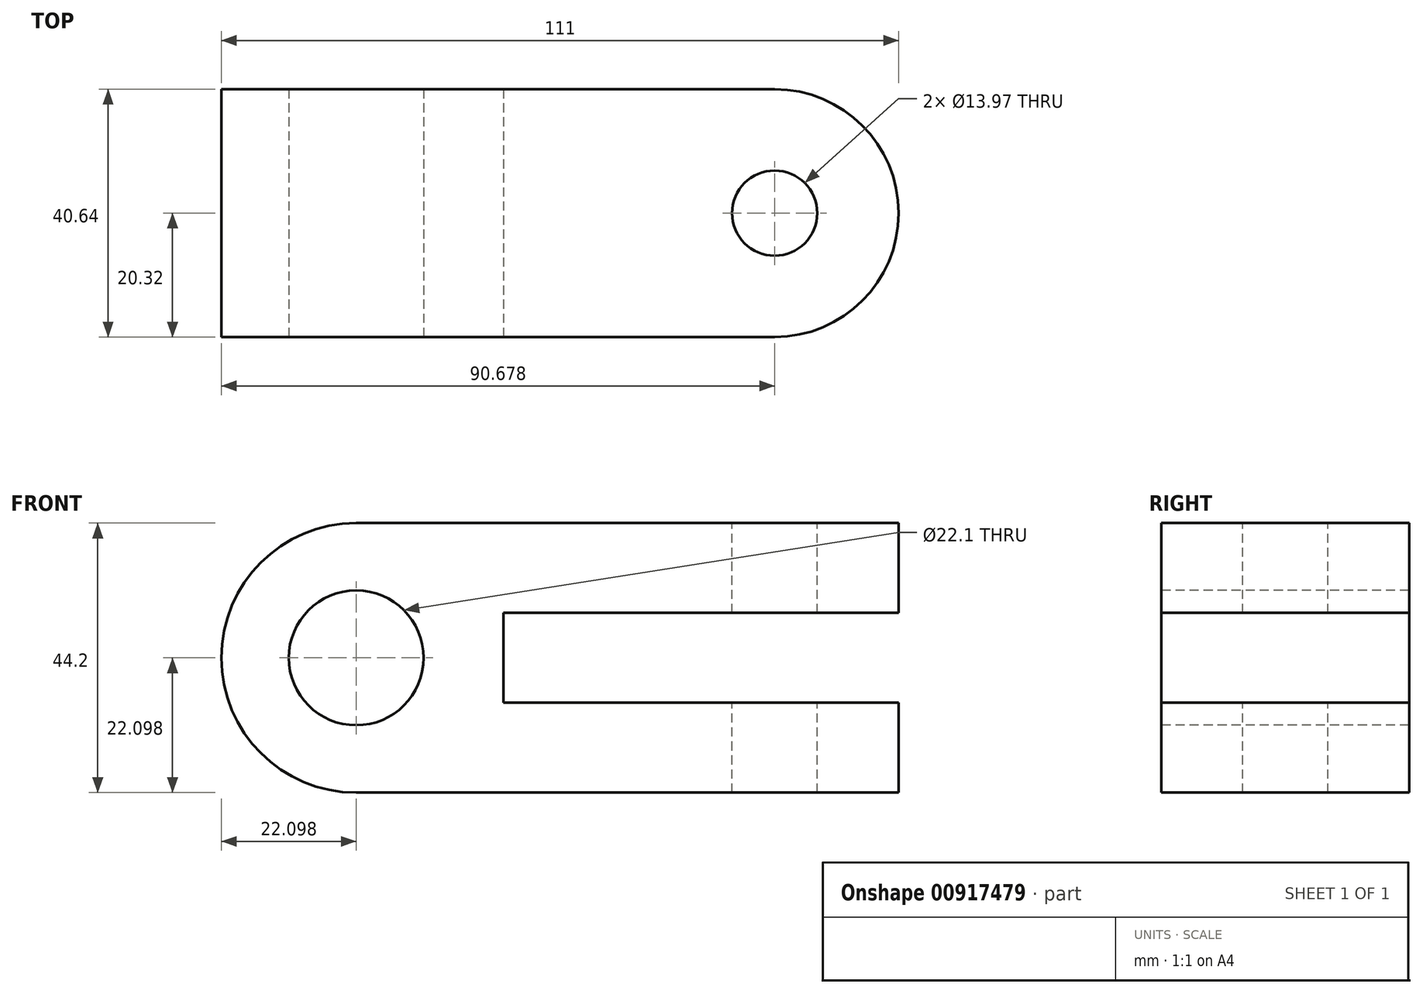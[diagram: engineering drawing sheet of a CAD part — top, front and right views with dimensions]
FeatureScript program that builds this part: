
annotation { "Feature Type Name" : "Feature", "Feature Type Description" : "" }
export const myFeature = defineFeature(function(context is Context, id is Id, definition is map)
    precondition{}
    {
        {
            var Q0;
            Q0=qCreatedBy(makeId("Top.planeOp"),FACE);
            var sketch = newSketch(context, id + "F0", { "sketchPlane" : qUnion([Q0])});
            skLineSegment(sketch, "E0.bottom", {"start": v(0, 0) * mm, "end": v(111, 0) * mm});
            skLineSegment(sketch, "E0.top", {"start": v(0, 40.64) * mm, "end": v(111, 40.64) * mm});
            skLineSegment(sketch, "E0.left", {"start": v(0, 0) * mm, "end": v(0, 40.64) * mm});
            skLineSegment(sketch, "E0.right", {"start": v(111, 0) * mm, "end": v(111, 40.64) * mm});
            skSolve(sketch);
        }
        {
            var Q0;
            Q0=makeQuery(id+"F0.imprint","IMPRINT",FACE,{"disambiguationData":[TD([[makeQuery(id+"F0.imprint","IMPRINT",EDGE,{"derivedFrom":sQuery(id+"F0.wireOp",EDGE,"E0.bottom")}),1.0]])]});
            extrude(context, id + "F1", {"entities" : qUnion([Q0]), "depth" : 44.2 * mm, "offsetDistance" : 25.4 * mm});
        }
        {
            var Q0;
            Q0=makeQuery(id+"F1.opExtrude","CAP_FACE",FACE,{"disambiguationData":[OSD([sQuery(id+"F0.wireOp",EDGE,"E0.bottom"),sQuery(id+"F0.wireOp",EDGE,"E0.top"),sQuery(id+"F0.wireOp",EDGE,"E0.left"),sQuery(id+"F0.wireOp",EDGE,"E0.right")])],"isStart":false});
            var sketch = newSketch(context, id + "F2", { "sketchPlane" : qUnion([Q0])});
            skCircle(sketch, "E1", {"center": v(90.68, 20.32) * mm, "radius": 20.32 * mm});
            skCircle(sketch, "E2", {"center": v(90.68, 20.32) * mm, "radius": 6.99 * mm});
            skSolve(sketch);
        }
        {
            var Q0;
            Q0=makeQuery(id+"F1.opExtrude","SWEPT_FACE",FACE,{"disambiguationData":[OSD([sQuery(id+"F0.wireOp",EDGE,"E0.bottom")])]});
            var sketch = newSketch(context, id + "F3", { "sketchPlane" : qUnion([Q0])});
            skCircle(sketch, "E3", {"center": v(22.1, 22.1) * mm, "radius": 22.1 * mm});
            skLineSegment(sketch, "E4", {"start": v(111, 29.46) * mm, "end": v(46.23, 29.46) * mm});
            skLineSegment(sketch, "E5", {"start": v(111, 14.73) * mm, "end": v(46.23, 14.73) * mm});
            skLineSegment(sketch, "E6", {"start": v(46.23, 14.73) * mm, "end": v(46.23, 29.62) * mm});
            skSolve(sketch);
        }
        {
            var Q0;
            Q0=makeQuery(id+"F1.opExtrude","SWEPT_FACE",FACE,{"disambiguationData":[OSD([sQuery(id+"F0.wireOp",EDGE,"E0.bottom")])]});
            var sketch = newSketch(context, id + "F4", { "sketchPlane" : qUnion([Q0])});
            skPoint(sketch, "E7", {"position": v(22.1, 22.1) * mm});
            skSolve(sketch);
        }
        {
            var Q0;
            Q0=sQuery(id+"F4.wireOp",VERTEX,"E7");
            var Q1;
            Q1=makeQuery(id+"F1.opExtrude","SWEPT_BODY",BODY,{"disambiguationData":[OSD([sQuery(id+"F0.wireOp",EDGE,"E0.bottom"),sQuery(id+"F0.wireOp",EDGE,"E0.top"),sQuery(id+"F0.wireOp",EDGE,"E0.left"),sQuery(id+"F0.wireOp",EDGE,"E0.right")])]});
            hole(context, id + "F5", {"style" : HoleStyle.SIMPLE, "endStyle" : HoleEndStyle.THROUGH, "holeDiameter" : 22.1 * mm, "majorDiameter" : 6.35 * mm, "isTappedThrough" : true, "tappedDepth" : 12.7 * mm, "tapClearance" : 3, "locations" : qUnion([Q0]), "scope" : qUnion([Q1])});
        }
        {
            var Q0;
            Q0=makeQuery(id+"F2.imprint","IMPRINT",FACE,{"disambiguationData":[TD([[makeQuery(id+"F2.imprint","IMPRINT",EDGE,{"derivedFrom":sQuery(id+"F2.wireOp",EDGE,"E2")}),1.0]])]});
            var Q1;
            Q1=sQuery(id+"F2.wireOp",EDGE,"E2");
            extrude(context, id + "F6", {"entities" : qUnion([Q0]), "operationType" : NewBodyOperationType.REMOVE, "surfaceEntities" : qUnion([Q1]), "endBound" : BoundingType.THROUGH_ALL, "oppositeDirection" : true, "depth" : 25.4 * mm, "offsetDistance" : 25.4 * mm});
        }
        {
            var Q0;
            {var subQ0=sQuery(id+"F2.wireOp",EDGE,"E1");var subQ1=makeQuery(id+"F1.opExtrude","CAP_EDGE",EDGE,{"disambiguationData":[OSD([sQuery(id+"F0.wireOp",EDGE,"E0.top")])],"isStart":false});var subQ2=makeQuery(id+"F2.imprint","INTERSECT",VERTEX,{"derivedFrom":[subQ1,subQ0]});Q0=makeQuery(id+"F2.imprint","IMPRINT",FACE,{"disambiguationData":[TD([[makeQuery(id+"F2.imprint","IMPRINT",EDGE,{"disambiguationData":[TD([[subQ2,1.0]])],"derivedFrom":subQ0}),-1.0]])]});}
            var Q1;
            {var subQ0=sQuery(id+"F2.wireOp",EDGE,"E1");var subQ1=makeQuery(id+"F1.opExtrude","CAP_EDGE",EDGE,{"disambiguationData":[OSD([sQuery(id+"F0.wireOp",EDGE,"E0.right")])],"isStart":false});var subQ2=makeQuery(id+"F2.imprint","INTERSECT",VERTEX,{"derivedFrom":[subQ1,subQ0]});Q1=makeQuery(id+"F2.imprint","IMPRINT",FACE,{"disambiguationData":[TD([[makeQuery(id+"F2.imprint","IMPRINT",EDGE,{"disambiguationData":[TD([[subQ2,1.0]])],"derivedFrom":subQ0}),-1.0]])]});}
            extrude(context, id + "F7", {"entities" : qUnion([Q0, Q1]), "operationType" : NewBodyOperationType.REMOVE, "endBound" : BoundingType.THROUGH_ALL, "oppositeDirection" : true, "depth" : 25.4 * mm, "offsetDistance" : 25.4 * mm});
        }
        {
            var Q0;
            {var subQ0=sQuery(id+"F3.wireOp",EDGE,"E4");Q0=makeQuery(id+"F3.imprint","IMPRINT",FACE,{"disambiguationData":[TD([[makeQuery(id+"F3.imprint","IMPRINT",EDGE,{"derivedFrom":subQ0}),1.0]])]});}
            extrude(context, id + "F8", {"entities" : qUnion([Q0]), "operationType" : NewBodyOperationType.REMOVE, "endBound" : BoundingType.THROUGH_ALL, "oppositeDirection" : true, "depth" : 25.4 * mm, "offsetDistance" : 25.4 * mm});
        }
        {
            var Q0;
            {var subQ0=sQuery(id+"F3.wireOp",EDGE,"E3");var subQ1=sQuery(id+"F0.wireOp",EDGE,"E0.bottom");var subQ4=makeQuery(id+"F1.opExtrude","CAP_EDGE",EDGE,{"disambiguationData":[OSD([subQ1])],"isStart":false});var subQ5=makeQuery(id+"F3.imprint","INTERSECT",VERTEX,{"derivedFrom":[subQ4,subQ0]});Q0=makeQuery(id+"F3.imprint","IMPRINT",FACE,{"disambiguationData":[TD([[makeQuery(id+"F3.imprint","IMPRINT",EDGE,{"disambiguationData":[TD([[subQ5,-1.0]])],"derivedFrom":subQ0}),-1.0]])]});}
            var Q1;
            {var subQ0=sQuery(id+"F3.wireOp",EDGE,"E3");var subQ1=sQuery(id+"F0.wireOp",EDGE,"E0.bottom");var subQ4=makeQuery(id+"F1.opExtrude","CAP_EDGE",EDGE,{"disambiguationData":[OSD([subQ1])],"isStart":true});var subQ5=makeQuery(id+"F3.imprint","INTERSECT",VERTEX,{"derivedFrom":[subQ4,subQ0]});Q1=makeQuery(id+"F3.imprint","IMPRINT",FACE,{"disambiguationData":[TD([[makeQuery(id+"F3.imprint","IMPRINT",EDGE,{"disambiguationData":[TD([[subQ5,1.0]])],"derivedFrom":subQ0}),-1.0]])]});}
            extrude(context, id + "F9", {"entities" : qUnion([Q0, Q1]), "operationType" : NewBodyOperationType.REMOVE, "endBound" : BoundingType.THROUGH_ALL, "oppositeDirection" : true, "depth" : 25.4 * mm, "offsetDistance" : 25.4 * mm});
        }
    });
